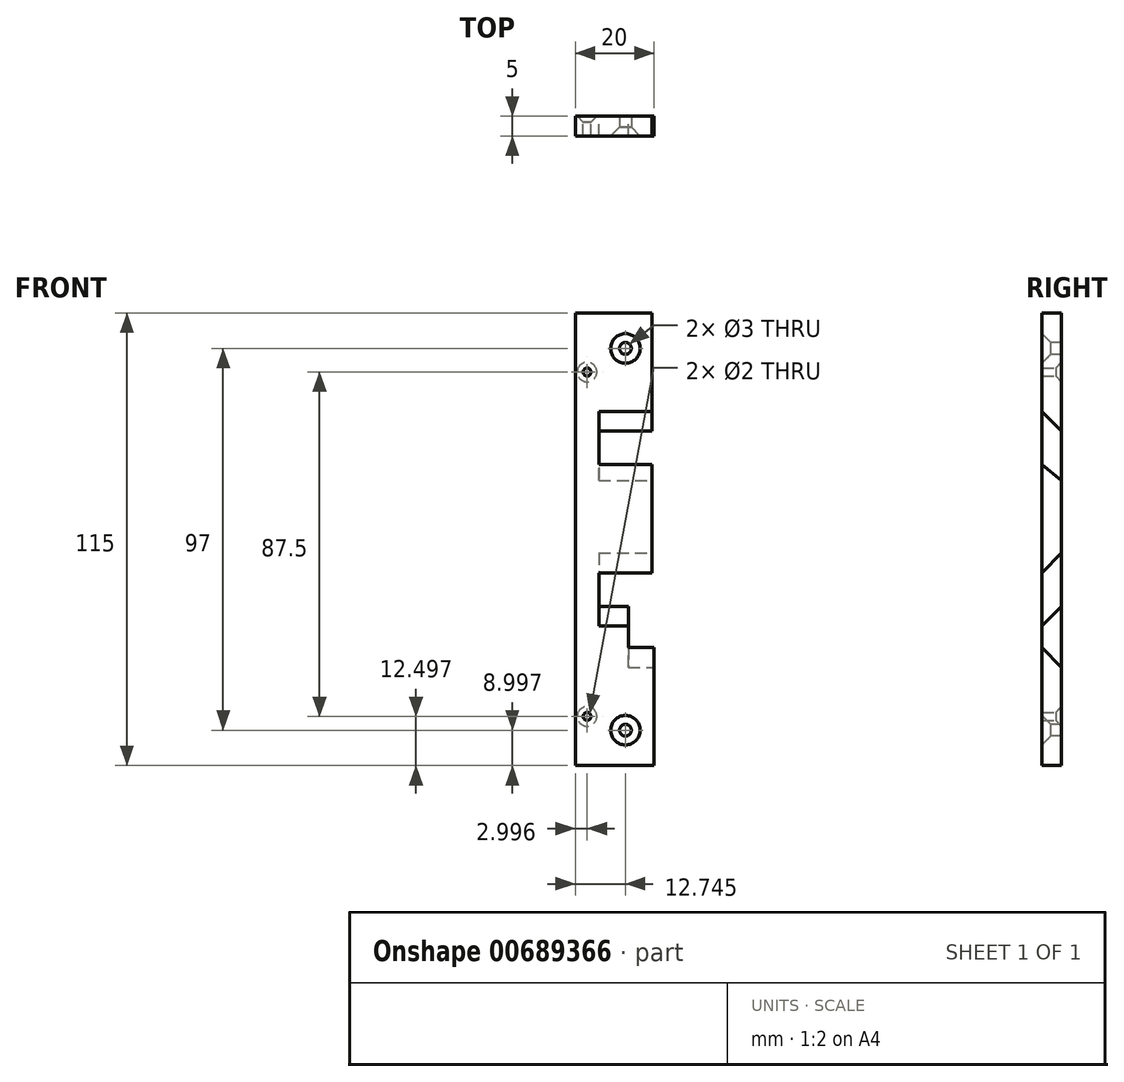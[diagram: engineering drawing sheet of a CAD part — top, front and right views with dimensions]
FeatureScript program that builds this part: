
annotation { "Feature Type Name" : "Feature", "Feature Type Description" : "" }
export const myFeature = defineFeature(function(context is Context, id is Id, definition is map)
    precondition{}
    {
        {
            var Q0;
            Q0=qCreatedBy(makeId("Front.planeOp"),FACE);
            var sketch = newSketch(context, id + "F0", { "sketchPlane" : qUnion([Q0])});
            skLineSegment(sketch, "E0.top", {"start": v(-0.37, 114.33) * mm, "end": v(19.13, 114.33) * mm});
            skLineSegment(sketch, "E0.left", {"start": v(-0.37, -0.67) * mm, "end": v(-0.37, 114.33) * mm});
            skLineSegment(sketch, "E1", {"start": v(5.63, 84.33) * mm, "end": v(5.63, 75.83) * mm});
            skLineSegment(sketch, "E2", {"start": v(5.63, 84.33) * mm, "end": v(19.13, 84.33) * mm});
            skLineSegment(sketch, "E3.trimOffspring", {"start": v(5.63, 48.33) * mm, "end": v(5.63, 39.83) * mm});
            skLineSegment(sketch, "E4", {"start": v(19.13, 114.33) * mm, "end": v(19.13, 84.33) * mm});
            skLineSegment(sketch, "E5.trimOffspring", {"start": v(19.13, 75.83) * mm, "end": v(5.63, 75.83) * mm});
            skLineSegment(sketch, "E6.trimOffspring", {"start": v(19.13, 48.33) * mm, "end": v(5.63, 48.33) * mm});
            skLineSegment(sketch, "E7.trimOffspring", {"start": v(19.63, 29.33) * mm, "end": v(13.13, 29.33) * mm});
            skLineSegment(sketch, "E8", {"start": v(19.63, 29.33) * mm, "end": v(19.63, -0.67) * mm});
            skLineSegment(sketch, "E9", {"start": v(13.13, 29.33) * mm, "end": v(13.13, 39.83) * mm});
            skLineSegment(sketch, "E10.trimOffspring", {"start": v(13.13, 39.83) * mm, "end": v(5.63, 39.83) * mm});
            skLineSegment(sketch, "E11.trimOffspring", {"start": v(19.13, 75.83) * mm, "end": v(19.13, 48.33) * mm});
            skLineSegment(sketch, "E12", {"start": v(-0.37, -0.67) * mm, "end": v(19.63, -0.67) * mm});
            skSolve(sketch);
        }
        {
            var Q0;
            Q0=qSketchRegion(id+"F0",true);
            extrude(context, id + "F1", {"entities" : qUnion([Q0]), "depth" : 5 * mm});
        }
        {
            var Q0;
            Q0=makeQuery(id+"F1.opExtrude","SWEPT_FACE",FACE,{"disambiguationData":[OSD([sQuery(id+"F0.wireOp",EDGE,"E4")])]});
            var sketch = newSketch(context, id + "F2", { "sketchPlane" : qUnion([Q0])});
            skLineSegment(sketch, "E13", {"start": v(0, 84.33) * mm, "end": v(-5, 84.33) * mm});
            skLineSegment(sketch, "E14", {"start": v(-5, 84.33) * mm, "end": v(-5, 89.33) * mm});
            skLineSegment(sketch, "E15", {"start": v(-5, 89.33) * mm, "end": v(0, 84.33) * mm});
            skSolve(sketch);
        }
        {
            var Q0;
            Q0=makeQuery(id+"F1.opExtrude","SWEPT_FACE",FACE,{"disambiguationData":[OSD([sQuery(id+"F0.wireOp",EDGE,"E11.trimOffspring")])]});
            var sketch = newSketch(context, id + "F3", { "sketchPlane" : qUnion([Q0])});
            skLineSegment(sketch, "E16", {"start": v(-5, 75.83) * mm, "end": v(0, 75.83) * mm});
            skLineSegment(sketch, "E17", {"start": v(0, 75.83) * mm, "end": v(0, 71.83) * mm});
            skLineSegment(sketch, "E18", {"start": v(0, 71.83) * mm, "end": v(-5, 75.83) * mm});
            skLineSegment(sketch, "E19", {"start": v(-5, 48.33) * mm, "end": v(0, 48.33) * mm});
            skLineSegment(sketch, "E20", {"start": v(0, 48.33) * mm, "end": v(0, 53.33) * mm});
            skLineSegment(sketch, "E21", {"start": v(0, 53.33) * mm, "end": v(-5, 48.33) * mm});
            skSolve(sketch);
        }
        {
            var Q0;
            Q0=qSketchRegion(id+"F2",true);
            var Q1;
            Q1=qSketchRegion(id+"F3",true);
            extrude(context, id + "F4", {"entities" : qUnion([Q0, Q1]), "operationType" : NewBodyOperationType.REMOVE, "oppositeDirection" : true, "depth" : 13.5 * mm});
        }
        {
            var Q0;
            Q0=makeQuery(id+"F1.opExtrude","SWEPT_FACE",FACE,{"disambiguationData":[OSD([sQuery(id+"F0.wireOp",EDGE,"E9")])]});
            var sketch = newSketch(context, id + "F5", { "sketchPlane" : qUnion([Q0])});
            skLineSegment(sketch, "E22", {"start": v(0, 39.83) * mm, "end": v(-5, 39.83) * mm});
            skLineSegment(sketch, "E23", {"start": v(-5, 39.83) * mm, "end": v(-5, 34.83) * mm});
            skLineSegment(sketch, "E24", {"start": v(-5, 34.83) * mm, "end": v(0, 39.83) * mm});
            skSolve(sketch);
        }
        {
            var Q0;
            Q0=qSketchRegion(id+"F5",true);
            extrude(context, id + "F6", {"entities" : qUnion([Q0]), "operationType" : NewBodyOperationType.REMOVE, "oppositeDirection" : true, "depth" : 7.5 * mm});
        }
        {
            var Q0;
            Q0=makeQuery(id+"F1.opExtrude","SWEPT_FACE",FACE,{"disambiguationData":[OSD([sQuery(id+"F0.wireOp",EDGE,"E8")])]});
            var sketch = newSketch(context, id + "F7", { "sketchPlane" : qUnion([Q0])});
            skLineSegment(sketch, "E25", {"start": v(0, 29.33) * mm, "end": v(-5, 29.33) * mm});
            skLineSegment(sketch, "E26", {"start": v(-5, 29.33) * mm, "end": v(0, 24.33) * mm});
            skLineSegment(sketch, "E27", {"start": v(0, 24.33) * mm, "end": v(0, 29.33) * mm});
            skSolve(sketch);
        }
        {
            var Q0;
            Q0=qSketchRegion(id+"F7",true);
            extrude(context, id + "F8", {"entities" : qUnion([Q0]), "operationType" : NewBodyOperationType.REMOVE, "oppositeDirection" : true, "depth" : 6.5 * mm});
        }
        {
            var Q0;
            Q0=makeQuery(id+"F1.opExtrude","CAP_FACE",FACE,{"disambiguationData":[OSD([sQuery(id+"F0.wireOp",EDGE,"E0.top"),sQuery(id+"F0.wireOp",EDGE,"E0.left"),sQuery(id+"F0.wireOp",EDGE,"E1"),sQuery(id+"F0.wireOp",EDGE,"E2"),sQuery(id+"F0.wireOp",EDGE,"E3.trimOffspring"),sQuery(id+"F0.wireOp",EDGE,"E4"),sQuery(id+"F0.wireOp",EDGE,"E5.trimOffspring"),sQuery(id+"F0.wireOp",EDGE,"E6.trimOffspring"),sQuery(id+"F0.wireOp",EDGE,"E7.trimOffspring"),sQuery(id+"F0.wireOp",EDGE,"E8"),sQuery(id+"F0.wireOp",EDGE,"E9"),sQuery(id+"F0.wireOp",EDGE,"E10.trimOffspring"),sQuery(id+"F0.wireOp",EDGE,"E11.trimOffspring"),sQuery(id+"F0.wireOp",EDGE,"E12")])],"isStart":false});
            var sketch = newSketch(context, id + "F9", { "sketchPlane" : qUnion([Q0])});
            skPoint(sketch, "E28", {"position": v(12.38, 105.33) * mm});
            skPoint(sketch, "E29", {"position": v(12.38, 8.33) * mm});
            skSolve(sketch);
        }
        {
            var Q0;
            Q0=sQuery(id+"F9.wireOp",VERTEX,"E28");
            var Q1;
            Q1=sQuery(id+"F9.wireOp",VERTEX,"E29");
            var Q2;
            Q2=makeQuery(id+"F1.opExtrude","SWEPT_BODY",BODY,{"disambiguationData":[OSD([sQuery(id+"F0.wireOp",EDGE,"E0.top"),sQuery(id+"F0.wireOp",EDGE,"E0.left"),sQuery(id+"F0.wireOp",EDGE,"E1"),sQuery(id+"F0.wireOp",EDGE,"E2"),sQuery(id+"F0.wireOp",EDGE,"E3.trimOffspring"),sQuery(id+"F0.wireOp",EDGE,"E4"),sQuery(id+"F0.wireOp",EDGE,"E5.trimOffspring"),sQuery(id+"F0.wireOp",EDGE,"E6.trimOffspring"),sQuery(id+"F0.wireOp",EDGE,"E7.trimOffspring"),sQuery(id+"F0.wireOp",EDGE,"E8"),sQuery(id+"F0.wireOp",EDGE,"E9"),sQuery(id+"F0.wireOp",EDGE,"E10.trimOffspring"),sQuery(id+"F0.wireOp",EDGE,"E11.trimOffspring"),sQuery(id+"F0.wireOp",EDGE,"E12")])]});
            hole(context, id + "F10", {"style" : HoleStyle.C_SINK, "endStyle" : HoleEndStyle.THROUGH, "holeDiameter" : 3 * mm, "cSinkDiameter" : 7.5 * mm, "cSinkAngle" : 90 * degree, "majorDiameter" : 5 * mm, "isTappedThrough" : true, "tappedDepth" : 12 * mm, "tapClearance" : 3, "startFromSketch" : true, "locations" : qUnion([Q0, Q1]), "scope" : qUnion([Q2])});
        }
        {
            var Q0;
            Q0=makeQuery(id+"F1.opExtrude","CAP_FACE",FACE,{"disambiguationData":[OSD([sQuery(id+"F0.wireOp",EDGE,"E0.top"),sQuery(id+"F0.wireOp",EDGE,"E0.left"),sQuery(id+"F0.wireOp",EDGE,"E1"),sQuery(id+"F0.wireOp",EDGE,"E2"),sQuery(id+"F0.wireOp",EDGE,"E3.trimOffspring"),sQuery(id+"F0.wireOp",EDGE,"E4"),sQuery(id+"F0.wireOp",EDGE,"E5.trimOffspring"),sQuery(id+"F0.wireOp",EDGE,"E6.trimOffspring"),sQuery(id+"F0.wireOp",EDGE,"E7.trimOffspring"),sQuery(id+"F0.wireOp",EDGE,"E8"),sQuery(id+"F0.wireOp",EDGE,"E9"),sQuery(id+"F0.wireOp",EDGE,"E10.trimOffspring"),sQuery(id+"F0.wireOp",EDGE,"E11.trimOffspring"),sQuery(id+"F0.wireOp",EDGE,"E12")])],"isStart":true});
            var sketch = newSketch(context, id + "F11", { "sketchPlane" : qUnion([Q0])});
            skPoint(sketch, "E30", {"position": v(-2.63, 11.83) * mm});
            skPoint(sketch, "E31", {"position": v(-2.63, 99.33) * mm});
            skSolve(sketch);
        }
        {
            var Q0;
            Q0=sQuery(id+"F11.wireOp",VERTEX,"E30");
            var Q1;
            Q1=sQuery(id+"F11.wireOp",VERTEX,"E31");
            var Q2;
            Q2=makeQuery(id+"F1.opExtrude","SWEPT_BODY",BODY,{"disambiguationData":[OSD([sQuery(id+"F0.wireOp",EDGE,"E0.top"),sQuery(id+"F0.wireOp",EDGE,"E0.left"),sQuery(id+"F0.wireOp",EDGE,"E1"),sQuery(id+"F0.wireOp",EDGE,"E2"),sQuery(id+"F0.wireOp",EDGE,"E3.trimOffspring"),sQuery(id+"F0.wireOp",EDGE,"E4"),sQuery(id+"F0.wireOp",EDGE,"E5.trimOffspring"),sQuery(id+"F0.wireOp",EDGE,"E6.trimOffspring"),sQuery(id+"F0.wireOp",EDGE,"E7.trimOffspring"),sQuery(id+"F0.wireOp",EDGE,"E8"),sQuery(id+"F0.wireOp",EDGE,"E9"),sQuery(id+"F0.wireOp",EDGE,"E10.trimOffspring"),sQuery(id+"F0.wireOp",EDGE,"E11.trimOffspring"),sQuery(id+"F0.wireOp",EDGE,"E12")])]});
            hole(context, id + "F12", {"style" : HoleStyle.C_SINK, "endStyle" : HoleEndStyle.THROUGH, "holeDiameter" : 2 * mm, "cSinkDiameter" : 5 * mm, "cSinkAngle" : 90 * degree, "majorDiameter" : 5 * mm, "isTappedThrough" : true, "tappedDepth" : 12 * mm, "tapClearance" : 3, "startFromSketch" : true, "locations" : qUnion([Q0, Q1]), "scope" : qUnion([Q2])});
        }
    });
